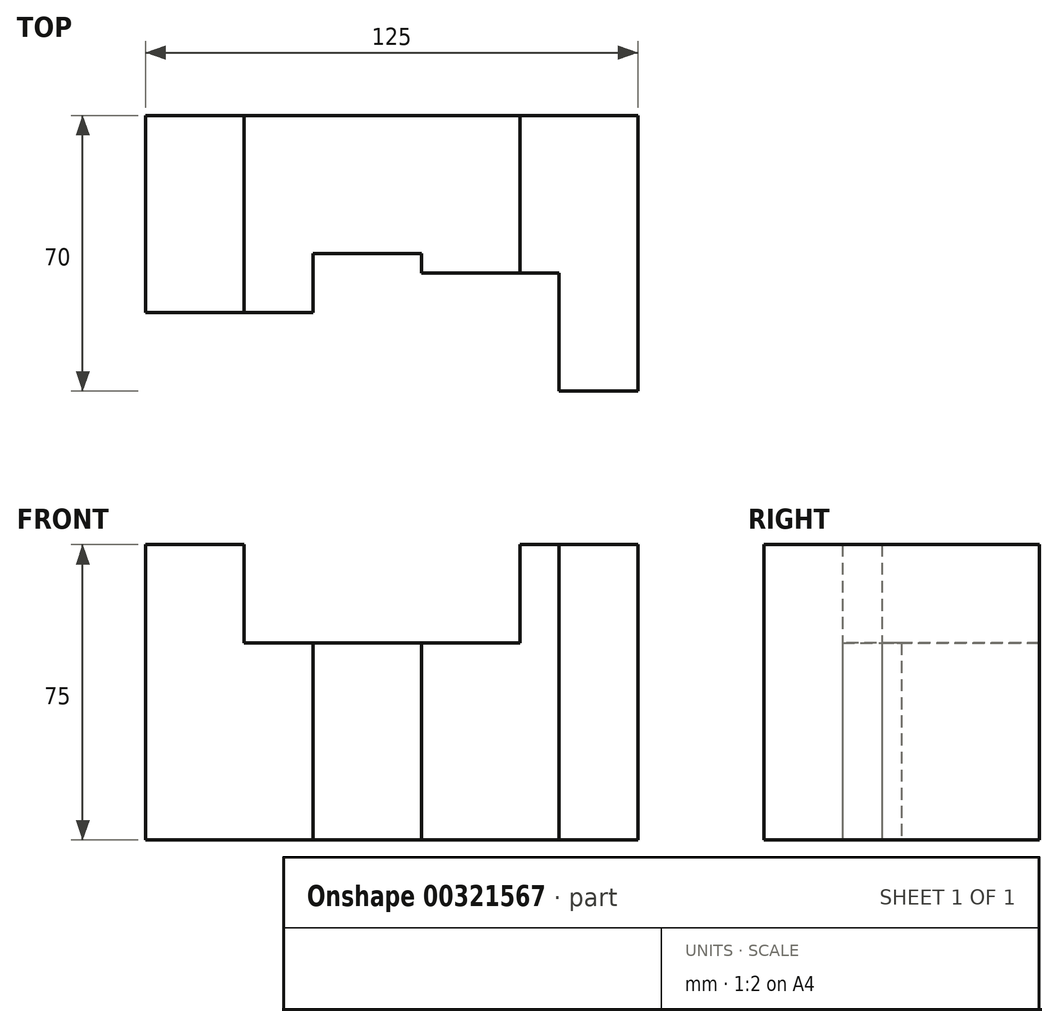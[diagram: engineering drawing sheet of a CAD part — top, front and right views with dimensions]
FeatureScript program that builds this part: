
annotation { "Feature Type Name" : "Feature", "Feature Type Description" : "" }
export const myFeature = defineFeature(function(context is Context, id is Id, definition is map)
    precondition{}
    {
        {
            var Q0;
            Q0=qCreatedBy(makeId("Top.planeOp"),FACE);
            var sketch = newSketch(context, id + "F0", { "sketchPlane" : qUnion([Q0])});
            skLineSegment(sketch, "E0.bottom", {"start": v(0, 0) * mm, "end": v(20, 0) * mm});
            skLineSegment(sketch, "E0.right", {"start": v(20, 0) * mm, "end": v(20, 70) * mm});
            skLineSegment(sketch, "E1", {"start": v(0, 0) * mm, "end": v(0, 30) * mm});
            skLineSegment(sketch, "E2", {"start": v(0, 30) * mm, "end": v(-10, 30) * mm});
            skLineSegment(sketch, "E3", {"start": v(-10, 30) * mm, "end": v(-10, 70) * mm});
            skLineSegment(sketch, "E4", {"start": v(-10, 70) * mm, "end": v(20, 70) * mm});
            skSolve(sketch);
        }
        {
            var Q0;
            Q0=makeQuery(id+"F0.imprint","IMPRINT",FACE,{"disambiguationData":[TD([[makeQuery(id+"F0.imprint","IMPRINT",EDGE,{"derivedFrom":sQuery(id+"F0.wireOp",EDGE,"E0.bottom")}),1.0]])]});
            extrude(context, id + "F1", {"entities" : qUnion([Q0]), "depth" : 75 * mm});
        }
        {
            var Q0;
            Q0=qCreatedBy(makeId("Top.planeOp"),FACE);
            var sketch = newSketch(context, id + "F2", { "sketchPlane" : qUnion([Q0])});
            skLineSegment(sketch, "E5", {"start": v(-10, 70) * mm, "end": v(-80, 70) * mm});
            skLineSegment(sketch, "E6", {"start": v(-80, 70) * mm, "end": v(-80, 20) * mm});
            skLineSegment(sketch, "E7", {"start": v(-80, 20) * mm, "end": v(-62.5, 20) * mm});
            skLineSegment(sketch, "E8", {"start": v(-62.5, 20) * mm, "end": v(-62.5, 35) * mm});
            skLineSegment(sketch, "E9", {"start": v(-62.5, 35) * mm, "end": v(-35, 35) * mm});
            skLineSegment(sketch, "E10", {"start": v(-35, 35) * mm, "end": v(-35, 30) * mm});
            skLineSegment(sketch, "E11", {"start": v(-35, 30) * mm, "end": v(-10, 30) * mm});
            skLineSegment(sketch, "E12", {"start": v(-10, 30) * mm, "end": v(-10, 70) * mm});
            skSolve(sketch);
        }
        {
            var Q0;
            Q0=makeQuery(id+"F2.imprint","IMPRINT",FACE,{"disambiguationData":[TD([[makeQuery(id+"F2.imprint","IMPRINT",EDGE,{"derivedFrom":sQuery(id+"F2.wireOp",EDGE,"E5")}),1.0]])]});
            extrude(context, id + "F3", {"entities" : qUnion([Q0]), "operationType" : NewBodyOperationType.ADD, "depth" : 50 * mm});
        }
        {
            var Q0;
            Q0=qCreatedBy(makeId("Top.planeOp"),FACE);
            var sketch = newSketch(context, id + "F4", { "sketchPlane" : qUnion([Q0])});
            skLineSegment(sketch, "E13.bottom", {"start": v(-80, 70) * mm, "end": v(-105, 70) * mm});
            skLineSegment(sketch, "E13.top", {"start": v(-80, 20) * mm, "end": v(-105, 20) * mm});
            skLineSegment(sketch, "E13.left", {"start": v(-80, 70) * mm, "end": v(-80, 20) * mm});
            skLineSegment(sketch, "E13.right", {"start": v(-105, 70) * mm, "end": v(-105, 20) * mm});
            skSolve(sketch);
        }
        {
            var Q0;
            Q0=makeQuery(id+"F4.imprint","IMPRINT",FACE,{"disambiguationData":[TD([[makeQuery(id+"F4.imprint","IMPRINT",EDGE,{"derivedFrom":sQuery(id+"F4.wireOp",EDGE,"E13.bottom")}),1.0]])]});
            extrude(context, id + "F5", {"entities" : qUnion([Q0]), "operationType" : NewBodyOperationType.ADD, "depth" : 75 * mm});
        }
    });
